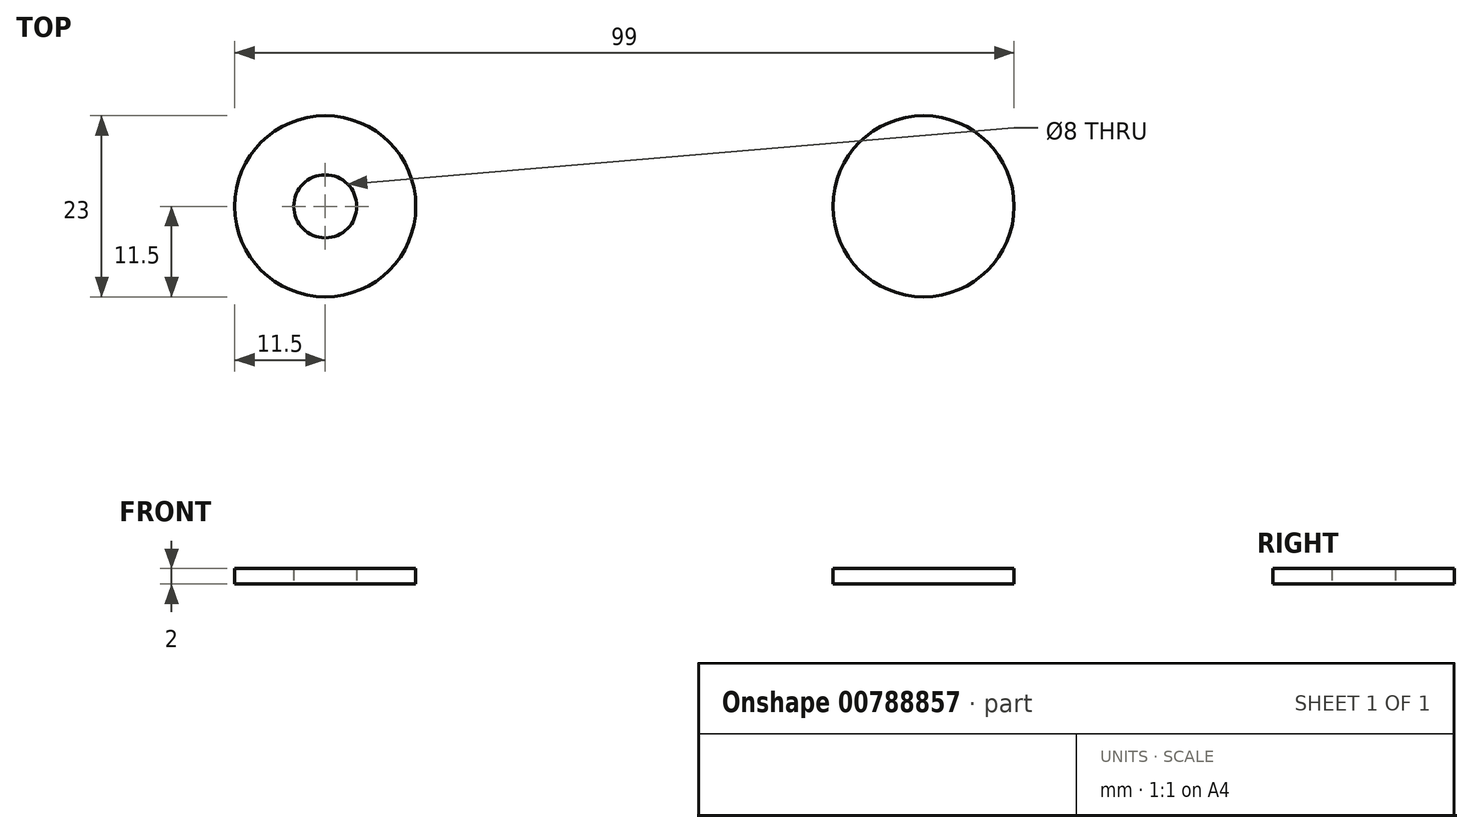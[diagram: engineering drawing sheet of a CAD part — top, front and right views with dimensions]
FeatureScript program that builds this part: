
annotation { "Feature Type Name" : "Feature", "Feature Type Description" : "" }
export const myFeature = defineFeature(function(context is Context, id is Id, definition is map)
    precondition{}
    {
        {
            var Q0;
            Q0=qCreatedBy(makeId("Top.planeOp"),FACE);
            var sketch = newSketch(context, id + "F0", { "sketchPlane" : qUnion([Q0])});
            skLineSegment(sketch, "E0", {"start": v(0, 0) * mm, "end": v(38, 0) * mm});
            skCircle(sketch, "E1", {"center": v(38, 0) * mm, "radius": 4 * mm});
            skCircle(sketch, "E2", {"center": v(38, 0) * mm, "radius": 11.5 * mm});
            skCircle(sketch, "E3.MirrorC", {"center": v(-38, 0) * mm, "radius": 4 * mm});
            skCircle(sketch, "E4.MirrorC", {"center": v(-38, 0) * mm, "radius": 11.5 * mm});
            skSolve(sketch);
        }
        {
            var Q0;
            Q0 = qSketchRegion(id + "F0", true);
            var Q1;
            Q1=makeQuery(id+"F0.imprint","IMPRINT",FACE,{"disambiguationData":[TD([[makeQuery(id+"F0.imprint","IMPRINT",EDGE,{"derivedFrom":sQuery(id+"F0.wireOp",EDGE,"E3.MirrorC")}),-1.0]])]});
            var Q2;
            Q2=makeQuery(id+"F0.imprint","IMPRINT",FACE,{"disambiguationData":[TD([[makeQuery(id+"F0.imprint","IMPRINT",EDGE,{"derivedFrom":sQuery(id+"F0.wireOp",EDGE,"E1")}),1.0]])]});
            extrude(context, id + "F1", {"entities" : qUnion([Q0, Q1, Q2]), "depth" : 2 * mm, "offsetDistance" : 25 * mm});
        }
        {
            var Q0;
            Q0=sQuery(id+"F0.wireOp",EDGE,"E3.MirrorC");
            var Q1;
            Q1=sQuery(id+"F0.wireOp",EDGE,"E1");
            extrude(context, id + "F2", {"bodyType" : ToolBodyType.SURFACE, "surfaceEntities" : qUnion([Q0, Q1]), "depth" : 7 * mm, "offsetDistance" : 25 * mm});
        }
    });
